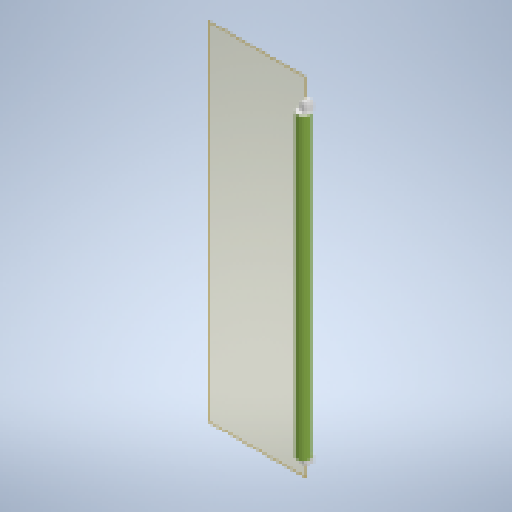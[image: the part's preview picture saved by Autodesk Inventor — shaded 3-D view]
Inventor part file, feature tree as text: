
AUTODESK INVENTOR PART (.ipt)
format: ipt  version: 2023 (Build 270158030, 158C)  size: 174,080 bytes
history: native  units: mm
features: other x4, extrude x2, sketch x2, reference x2, plane x1, fillet x1
ambient origin geometry x8: Origin, YZ Plane, XZ Plane, XY Plane, X Axis, Y Axis, Z Axis, Center Point
bodies: Solid1 (feature_tree)
feature tree (12):
  plane  "Work Plane1"
  extrude  "Extrusion1"  Depth=50.0mm
  fillet  "Fillet1"  Radius=50.0mm
  extrude  "Extrusion2"  Depth=20.0mm
  sketch  "Sketch1"  dims[d0=50.0mm d1=50.0mm d2=50.0mm]
  reference  "Reference1"
  sketch  "Sketch2"  dims[d3=50.0mm d4=0.0mm d5=20.0mm d6=40.0mm d7=25.0mm d8=75.0mm d9=50.0mm d10=0.0mm]
  reference  "Reference2"
  other  "canvas-top-stowed"
  other  "primary-engineer-bench.iam"
  other  "bed-base:1"
  other  "bench-slats:1"
